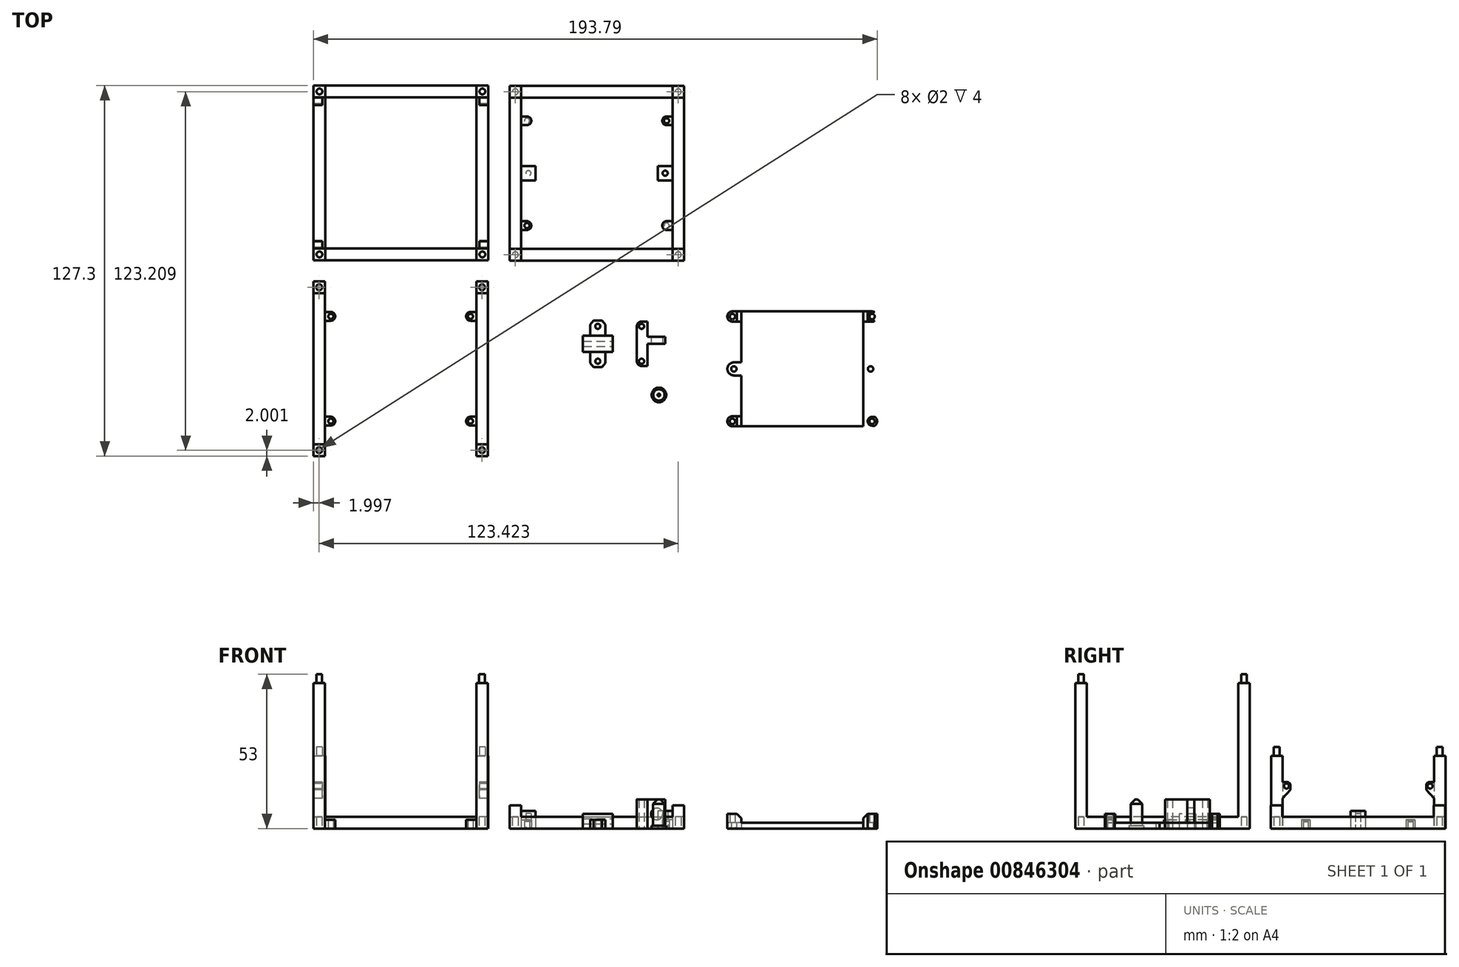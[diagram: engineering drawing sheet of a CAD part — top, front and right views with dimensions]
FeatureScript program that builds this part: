
annotation { "Feature Type Name" : "Feature", "Feature Type Description" : "" }
export const myFeature = defineFeature(function(context is Context, id is Id, definition is map)
    precondition{}
    {
        {
            var Q0;
            Q0=qCreatedBy(makeId("Top.planeOp"),FACE);
            var sketch = newSketch(context, id + "F0", { "sketchPlane" : qUnion([Q0])});
            skLineSegment(sketch, "E0.bottom", {"start": v(0, 60) * mm, "end": v(60, 60) * mm});
            skLineSegment(sketch, "E0.top", {"start": v(0, 0) * mm, "end": v(60, 0) * mm});
            skLineSegment(sketch, "E0.left", {"start": v(0, 60) * mm, "end": v(0, 0) * mm});
            skLineSegment(sketch, "E0.right", {"start": v(60, 60) * mm, "end": v(60, 0) * mm});
            skLineSegment(sketch, "E1.bottom", {"start": v(4, 56) * mm, "end": v(56, 56) * mm});
            skLineSegment(sketch, "E1.top", {"start": v(4, 4) * mm, "end": v(56, 4) * mm});
            skLineSegment(sketch, "E1.left", {"start": v(4, 56) * mm, "end": v(4, 4) * mm});
            skLineSegment(sketch, "E1.right", {"start": v(56, 56) * mm, "end": v(56, 4) * mm});
            skLineSegment(sketch, "E2", {"start": v(4, 56) * mm, "end": v(4, 60) * mm});
            skLineSegment(sketch, "E3", {"start": v(4, 56) * mm, "end": v(0, 56) * mm});
            skLineSegment(sketch, "E4", {"start": v(56, 56) * mm, "end": v(60, 56) * mm});
            skLineSegment(sketch, "E5", {"start": v(56, 56) * mm, "end": v(56, 60) * mm});
            skLineSegment(sketch, "E6", {"start": v(56, 4) * mm, "end": v(60, 4) * mm});
            skLineSegment(sketch, "E7", {"start": v(56, 4) * mm, "end": v(56, 0) * mm});
            skLineSegment(sketch, "E8", {"start": v(4, 4) * mm, "end": v(4, 0) * mm});
            skLineSegment(sketch, "E9", {"start": v(4, 4) * mm, "end": v(0, 4) * mm});
            skCircle(sketch, "E10", {"center": v(2, 58) * mm, "radius": 1 * mm});
            skPoint(sketch, "E10.centerSnap0", {"position": v(4, 58) * mm});
            skPoint(sketch, "E10.centerSnap1", {"position": v(2, 56) * mm});
            skCircle(sketch, "E11", {"center": v(58, 58) * mm, "radius": 1 * mm});
            skPoint(sketch, "E11.centerSnap0", {"position": v(56, 58) * mm});
            skPoint(sketch, "E11.centerSnap1", {"position": v(58, 56) * mm});
            skCircle(sketch, "E12", {"center": v(58, 2) * mm, "radius": 1 * mm});
            skPoint(sketch, "E12.centerSnap0", {"position": v(58, 4) * mm});
            skPoint(sketch, "E12.centerSnap1", {"position": v(56, 2) * mm});
            skCircle(sketch, "E13", {"center": v(2, 2) * mm, "radius": 1 * mm});
            skPoint(sketch, "E13.centerSnap0", {"position": v(2, 4) * mm});
            skPoint(sketch, "E13.centerSnap1", {"position": v(4, 2) * mm});
            skLineSegment(sketch, "E14", {"start": v(4, 49.5) * mm, "end": v(6, 49.5) * mm});
            skLineSegment(sketch, "E15", {"start": v(4, 46.5) * mm, "end": v(6, 46.5) * mm});
            skArc(sketch, "E16", {"start": v(6, 49.5) * mm, "mid": v(7.5, 48) * mm, "end": v(6, 46.5) * mm});
            skCircle(sketch, "E17", {"center": v(6, 48) * mm, "radius": 0.88 * mm});
            skPoint(sketch, "E18", {"position": v(4, 30) * mm});
            skLineSegment(sketch, "E19", {"start": v(-2.87, 30) * mm, "end": v(61.33, 30) * mm, "construction": true});
            skPoint(sketch, "E20", {"position": v(30, 56) * mm});
            skLineSegment(sketch, "E21", {"start": v(30, 61.27) * mm, "end": v(30, -1.45) * mm, "construction": true});
            skPoint(sketch, "E21.endSnap0", {"position": v(30, 0) * mm});
            skArc(sketch, "E22.MirrorCS", {"start": v(54, 49.5) * mm, "mid": v(52.5, 48) * mm, "end": v(54, 46.5) * mm});
            skLineSegment(sketch, "E23.MirrorCS", {"start": v(56, 46.5) * mm, "end": v(54, 46.5) * mm});
            skLineSegment(sketch, "E24.MirrorCS", {"start": v(56, 49.5) * mm, "end": v(54, 49.5) * mm});
            skCircle(sketch, "E25.MirrorC", {"center": v(54, 48) * mm, "radius": 0.88 * mm});
            skLineSegment(sketch, "E26.MirrorCS", {"start": v(56, 10.5) * mm, "end": v(54, 10.5) * mm});
            skLineSegment(sketch, "E27.MirrorCS", {"start": v(56, 13.5) * mm, "end": v(54, 13.5) * mm});
            skCircle(sketch, "E28.MirrorC", {"center": v(54, 12) * mm, "radius": 0.88 * mm});
            skArc(sketch, "E29.MirrorCS", {"start": v(54, 10.5) * mm, "mid": v(52.5, 12) * mm, "end": v(54, 13.5) * mm});
            skArc(sketch, "E30.MirrorCS", {"start": v(6, 10.5) * mm, "mid": v(7.5, 12) * mm, "end": v(6, 13.5) * mm});
            skLineSegment(sketch, "E31.MirrorCS", {"start": v(4, 13.5) * mm, "end": v(6, 13.5) * mm});
            skLineSegment(sketch, "E32.MirrorCS", {"start": v(4, 10.5) * mm, "end": v(6, 10.5) * mm});
            skCircle(sketch, "E33.MirrorC", {"center": v(6, 12) * mm, "radius": 0.88 * mm});
            skLineSegment(sketch, "E34", {"start": v(4, 32.5) * mm, "end": v(9, 32.5) * mm});
            skLineSegment(sketch, "E35", {"start": v(9, 32.5) * mm, "end": v(9, 30) * mm});
            skPoint(sketch, "E36", {"position": v(6.5, 32.5) * mm});
            skLineSegment(sketch, "E37.MirrorCS", {"start": v(9, 27.5) * mm, "end": v(9, 30) * mm});
            skLineSegment(sketch, "E38.MirrorCS", {"start": v(4, 27.5) * mm, "end": v(9, 27.5) * mm});
            skLineSegment(sketch, "E39.MirrorCS", {"start": v(56, 27.5) * mm, "end": v(51, 27.5) * mm});
            skLineSegment(sketch, "E40.MirrorCS", {"start": v(51, 27.5) * mm, "end": v(51, 30) * mm});
            skLineSegment(sketch, "E41.MirrorCS", {"start": v(56, 32.5) * mm, "end": v(51, 32.5) * mm});
            skLineSegment(sketch, "E42.MirrorCS", {"start": v(51, 32.5) * mm, "end": v(51, 30) * mm});
            skCircle(sketch, "E43", {"center": v(6.5, 30) * mm, "radius": 0.88 * mm});
            skCircle(sketch, "E44.MirrorC", {"center": v(53.5, 30) * mm, "radius": 0.88 * mm});
            skSolve(sketch);
        }
        {
            var Q0;
            Q0=makeQuery(id+"F0.imprint","IMPRINT",FACE,{"disambiguationData":[TD([[makeQuery(id+"F0.imprint","IMPRINT",EDGE,{"derivedFrom":sQuery(id+"F0.wireOp",EDGE,"E1.bottom")}),1.0]])]});
            var Q1;
            Q1=makeQuery(id+"F0.imprint","IMPRINT",FACE,{"disambiguationData":[TD([[makeQuery(id+"F0.imprint","IMPRINT",EDGE,{"derivedFrom":sQuery(id+"F0.wireOp",EDGE,"E1.right")}),1.0]])]});
            var Q2;
            {var subQ4=sQuery(id+"F0.wireOp",EDGE,"E6");Q2=makeQuery(id+"F0.imprint","IMPRINT",FACE,{"disambiguationData":[TD([[makeQuery(id+"F0.imprint","IMPRINT",EDGE,{"derivedFrom":subQ4}),-1.0]])]});}
            var Q3;
            {var subQ0=sQuery(id+"F0.wireOp",EDGE,"E8");Q3=makeQuery(id+"F0.imprint","IMPRINT",FACE,{"disambiguationData":[TD([[makeQuery(id+"F0.imprint","IMPRINT",EDGE,{"derivedFrom":subQ0}),-1.0]])]});}
            var Q4;
            Q4=makeQuery(id+"F0.imprint","IMPRINT",FACE,{"disambiguationData":[TD([[makeQuery(id+"F0.imprint","IMPRINT",EDGE,{"derivedFrom":sQuery(id+"F0.wireOp",EDGE,"E1.left")}),-1.0]])]});
            var Q5;
            Q5=makeQuery(id+"F0.imprint","IMPRINT",FACE,{"disambiguationData":[TD([[makeQuery(id+"F0.imprint","IMPRINT",EDGE,{"derivedFrom":sQuery(id+"F0.wireOp",EDGE,"E1.top")}),-1.0]])]});
            var Q6;
            {var subQ4=sQuery(id+"F0.wireOp",EDGE,"E2");Q6=makeQuery(id+"F0.imprint","IMPRINT",FACE,{"disambiguationData":[TD([[makeQuery(id+"F0.imprint","IMPRINT",EDGE,{"derivedFrom":subQ4}),1.0]])]});}
            var Q7;
            {var subQ0=sQuery(id+"F0.wireOp",EDGE,"E4");Q7=makeQuery(id+"F0.imprint","IMPRINT",FACE,{"disambiguationData":[TD([[makeQuery(id+"F0.imprint","IMPRINT",EDGE,{"derivedFrom":subQ0}),1.0]])]});}
            extrude(context, id + "F1", {"entities" : qUnion([Q0, Q1, Q2, Q3, Q4, Q5, Q6, Q7]), "depth" : 4 * mm, "offsetDistance" : 25 * mm});
        }
        {
            var Q0;
            {var subQ4=sQuery(id+"F0.wireOp",EDGE,"E6");Q0=makeQuery(id+"F0.imprint","IMPRINT",FACE,{"disambiguationData":[TD([[makeQuery(id+"F0.imprint","IMPRINT",EDGE,{"derivedFrom":subQ4}),-1.0]])]});}
            var Q1;
            Q1=makeQuery(id+"F0.imprint","IMPRINT",FACE,{"disambiguationData":[TD([[makeQuery(id+"F0.imprint","IMPRINT",EDGE,{"derivedFrom":sQuery(id+"F0.wireOp",EDGE,"E12")}),1.0]])]});
            var Q2;
            Q2=makeQuery(id+"F0.imprint","IMPRINT",FACE,{"disambiguationData":[TD([[makeQuery(id+"F0.imprint","IMPRINT",EDGE,{"derivedFrom":sQuery(id+"F0.wireOp",EDGE,"E13")}),1.0]])]});
            var Q3;
            {var subQ0=sQuery(id+"F0.wireOp",EDGE,"E8");Q3=makeQuery(id+"F0.imprint","IMPRINT",FACE,{"disambiguationData":[TD([[makeQuery(id+"F0.imprint","IMPRINT",EDGE,{"derivedFrom":subQ0}),-1.0]])]});}
            var Q4;
            Q4=makeQuery(id+"F0.imprint","IMPRINT",FACE,{"disambiguationData":[TD([[makeQuery(id+"F0.imprint","IMPRINT",EDGE,{"derivedFrom":sQuery(id+"F0.wireOp",EDGE,"E10")}),1.0]])]});
            var Q5;
            {var subQ4=sQuery(id+"F0.wireOp",EDGE,"E2");Q5=makeQuery(id+"F0.imprint","IMPRINT",FACE,{"disambiguationData":[TD([[makeQuery(id+"F0.imprint","IMPRINT",EDGE,{"derivedFrom":subQ4}),1.0]])]});}
            var Q6;
            {var subQ0=sQuery(id+"F0.wireOp",EDGE,"E4");Q6=makeQuery(id+"F0.imprint","IMPRINT",FACE,{"disambiguationData":[TD([[makeQuery(id+"F0.imprint","IMPRINT",EDGE,{"derivedFrom":subQ0}),1.0]])]});}
            var Q7;
            Q7=makeQuery(id+"F0.imprint","IMPRINT",FACE,{"disambiguationData":[TD([[makeQuery(id+"F0.imprint","IMPRINT",EDGE,{"derivedFrom":sQuery(id+"F0.wireOp",EDGE,"E11")}),1.0]])]});
            extrude(context, id + "F2", {"entities" : qUnion([Q0, Q1, Q2, Q3, Q4, Q5, Q6, Q7]), "operationType" : NewBodyOperationType.ADD, "depth" : 8 * mm, "offsetDistance" : 25 * mm});
        }
        {
            var Q0;
            Q0=qCreatedBy(makeId("Top.planeOp"),FACE);
            var sketch = newSketch(context, id + "F3", { "sketchPlane" : qUnion([Q0])});
            skLineSegment(sketch, "E45.bottom", {"start": v(-67.33, 60.09) * mm, "end": v(-7.33, 60.09) * mm});
            skLineSegment(sketch, "E45.top", {"start": v(-67.33, 0.09) * mm, "end": v(-7.33, 0.09) * mm});
            skLineSegment(sketch, "E45.left", {"start": v(-67.33, 60.09) * mm, "end": v(-67.33, 0.09) * mm});
            skLineSegment(sketch, "E45.right", {"start": v(-7.33, 60.09) * mm, "end": v(-7.33, 0.09) * mm});
            skLineSegment(sketch, "E46.bottom", {"start": v(-63.33, 56.09) * mm, "end": v(-11.33, 56.09) * mm});
            skLineSegment(sketch, "E46.top", {"start": v(-63.33, 4.09) * mm, "end": v(-11.33, 4.09) * mm});
            skLineSegment(sketch, "E46.left", {"start": v(-63.33, 56.09) * mm, "end": v(-63.33, 4.09) * mm});
            skLineSegment(sketch, "E46.right", {"start": v(-11.33, 56.09) * mm, "end": v(-11.33, 4.09) * mm});
            skLineSegment(sketch, "E47", {"start": v(-63.33, 56.09) * mm, "end": v(-63.33, 60.09) * mm});
            skLineSegment(sketch, "E48", {"start": v(-63.33, 56.09) * mm, "end": v(-67.33, 56.09) * mm});
            skLineSegment(sketch, "E49", {"start": v(-11.33, 56.09) * mm, "end": v(-7.33, 56.09) * mm});
            skLineSegment(sketch, "E50", {"start": v(-11.33, 56.09) * mm, "end": v(-11.33, 60.09) * mm});
            skLineSegment(sketch, "E51", {"start": v(-11.33, 4.09) * mm, "end": v(-7.33, 4.09) * mm});
            skLineSegment(sketch, "E52", {"start": v(-11.33, 4.09) * mm, "end": v(-11.33, 0.09) * mm});
            skLineSegment(sketch, "E53", {"start": v(-63.33, 4.09) * mm, "end": v(-63.33, 0.09) * mm});
            skLineSegment(sketch, "E54", {"start": v(-63.33, 4.09) * mm, "end": v(-67.33, 4.09) * mm});
            skCircle(sketch, "E55", {"center": v(-65.33, 58.09) * mm, "radius": 1 * mm});
            skPoint(sketch, "E55.centerSnap0", {"position": v(-63.33, 58.09) * mm});
            skPoint(sketch, "E55.centerSnap1", {"position": v(-65.33, 56.09) * mm});
            skCircle(sketch, "E56", {"center": v(-9.33, 58.09) * mm, "radius": 1 * mm});
            skPoint(sketch, "E56.centerSnap0", {"position": v(-11.33, 58.09) * mm});
            skPoint(sketch, "E56.centerSnap1", {"position": v(-9.33, 56.09) * mm});
            skCircle(sketch, "E57", {"center": v(-9.33, 2.09) * mm, "radius": 1 * mm});
            skPoint(sketch, "E57.centerSnap0", {"position": v(-9.33, 4.09) * mm});
            skPoint(sketch, "E57.centerSnap1", {"position": v(-11.33, 2.09) * mm});
            skCircle(sketch, "E58", {"center": v(-65.33, 2.09) * mm, "radius": 1 * mm});
            skPoint(sketch, "E58.centerSnap0", {"position": v(-65.33, 4.09) * mm});
            skPoint(sketch, "E58.centerSnap1", {"position": v(-63.33, 2.09) * mm});
            skSolve(sketch);
        }
        {
            var Q0;
            {var subQ0=sQuery(id+"F3.wireOp",EDGE,"E49");Q0=makeQuery(id+"F3.imprint","IMPRINT",FACE,{"disambiguationData":[TD([[makeQuery(id+"F3.imprint","IMPRINT",EDGE,{"derivedFrom":subQ0}),1.0]])]});}
            var Q1;
            Q1=makeQuery(id+"F3.imprint","IMPRINT",FACE,{"disambiguationData":[TD([[makeQuery(id+"F3.imprint","IMPRINT",EDGE,{"derivedFrom":sQuery(id+"F3.wireOp",EDGE,"E46.right")}),1.0]])]});
            var Q2;
            {var subQ4=sQuery(id+"F3.wireOp",EDGE,"E51");Q2=makeQuery(id+"F3.imprint","IMPRINT",FACE,{"disambiguationData":[TD([[makeQuery(id+"F3.imprint","IMPRINT",EDGE,{"derivedFrom":subQ4}),-1.0]])]});}
            var Q3;
            {var subQ0=sQuery(id+"F3.wireOp",EDGE,"E53");Q3=makeQuery(id+"F3.imprint","IMPRINT",FACE,{"disambiguationData":[TD([[makeQuery(id+"F3.imprint","IMPRINT",EDGE,{"derivedFrom":subQ0}),-1.0]])]});}
            var Q4;
            Q4=makeQuery(id+"F3.imprint","IMPRINT",FACE,{"disambiguationData":[TD([[makeQuery(id+"F3.imprint","IMPRINT",EDGE,{"derivedFrom":sQuery(id+"F3.wireOp",EDGE,"E46.left")}),-1.0]])]});
            var Q5;
            {var subQ4=sQuery(id+"F3.wireOp",EDGE,"E47");Q5=makeQuery(id+"F3.imprint","IMPRINT",FACE,{"disambiguationData":[TD([[makeQuery(id+"F3.imprint","IMPRINT",EDGE,{"derivedFrom":subQ4}),1.0]])]});}
            var Q6;
            Q6=makeQuery(id+"F3.imprint","IMPRINT",FACE,{"disambiguationData":[TD([[makeQuery(id+"F3.imprint","IMPRINT",EDGE,{"derivedFrom":sQuery(id+"F3.wireOp",EDGE,"E46.top")}),-1.0]])]});
            var Q7;
            Q7=makeQuery(id+"F3.imprint","IMPRINT",FACE,{"disambiguationData":[TD([[makeQuery(id+"F3.imprint","IMPRINT",EDGE,{"derivedFrom":sQuery(id+"F3.wireOp",EDGE,"E46.bottom")}),1.0]])]});
            extrude(context, id + "F4", {"entities" : qUnion([Q0, Q1, Q2, Q3, Q4, Q5, Q6, Q7]), "depth" : 4 * mm, "offsetDistance" : 25 * mm});
        }
        {
            var Q0;
            {var subQ0=sQuery(id+"F3.wireOp",EDGE,"E49");Q0=makeQuery(id+"F3.imprint","IMPRINT",FACE,{"disambiguationData":[TD([[makeQuery(id+"F3.imprint","IMPRINT",EDGE,{"derivedFrom":subQ0}),1.0]])]});}
            var Q1;
            {var subQ4=sQuery(id+"F3.wireOp",EDGE,"E47");Q1=makeQuery(id+"F3.imprint","IMPRINT",FACE,{"disambiguationData":[TD([[makeQuery(id+"F3.imprint","IMPRINT",EDGE,{"derivedFrom":subQ4}),1.0]])]});}
            var Q2;
            {var subQ0=sQuery(id+"F3.wireOp",EDGE,"E53");Q2=makeQuery(id+"F3.imprint","IMPRINT",FACE,{"disambiguationData":[TD([[makeQuery(id+"F3.imprint","IMPRINT",EDGE,{"derivedFrom":subQ0}),-1.0]])]});}
            var Q3;
            {var subQ4=sQuery(id+"F3.wireOp",EDGE,"E51");Q3=makeQuery(id+"F3.imprint","IMPRINT",FACE,{"disambiguationData":[TD([[makeQuery(id+"F3.imprint","IMPRINT",EDGE,{"derivedFrom":subQ4}),-1.0]])]});}
            extrude(context, id + "F5", {"entities" : qUnion([Q0, Q1, Q2, Q3]), "operationType" : NewBodyOperationType.ADD, "depth" : 25 * mm, "offsetDistance" : 25 * mm});
        }
        {
            var Q0;
            Q0=makeQuery(id+"F3.imprint","IMPRINT",FACE,{"disambiguationData":[TD([[makeQuery(id+"F3.imprint","IMPRINT",EDGE,{"derivedFrom":sQuery(id+"F3.wireOp",EDGE,"E56")}),1.0]])]});
            var Q1;
            Q1=makeQuery(id+"F3.imprint","IMPRINT",FACE,{"disambiguationData":[TD([[makeQuery(id+"F3.imprint","IMPRINT",EDGE,{"derivedFrom":sQuery(id+"F3.wireOp",EDGE,"E57")}),1.0]])]});
            var Q2;
            Q2=makeQuery(id+"F3.imprint","IMPRINT",FACE,{"disambiguationData":[TD([[makeQuery(id+"F3.imprint","IMPRINT",EDGE,{"derivedFrom":sQuery(id+"F3.wireOp",EDGE,"E58")}),1.0]])]});
            var Q3;
            Q3=makeQuery(id+"F3.imprint","IMPRINT",FACE,{"disambiguationData":[TD([[makeQuery(id+"F3.imprint","IMPRINT",EDGE,{"derivedFrom":sQuery(id+"F3.wireOp",EDGE,"E55")}),1.0]])]});
            extrude(context, id + "F6", {"entities" : qUnion([Q0, Q1, Q2, Q3]), "operationType" : NewBodyOperationType.ADD, "depth" : 28 * mm, "offsetDistance" : 25 * mm});
        }
        {
            var Q0;
            Q0=qCreatedBy(makeId("Top.planeOp"),FACE);
            var sketch = newSketch(context, id + "F7", { "sketchPlane" : qUnion([Q0])});
            skLineSegment(sketch, "E59.bottom", {"start": v(-67.42, -7.2) * mm, "end": v(-7.42, -7.2) * mm});
            skLineSegment(sketch, "E59.top", {"start": v(-67.42, -67.2) * mm, "end": v(-7.42, -67.2) * mm});
            skLineSegment(sketch, "E59.left", {"start": v(-67.42, -7.2) * mm, "end": v(-67.42, -67.2) * mm});
            skLineSegment(sketch, "E59.right", {"start": v(-7.42, -7.2) * mm, "end": v(-7.42, -67.2) * mm});
            skLineSegment(sketch, "E60.bottom", {"start": v(-63.42, -11.2) * mm, "end": v(-11.42, -11.2) * mm});
            skLineSegment(sketch, "E60.top", {"start": v(-63.42, -63.2) * mm, "end": v(-11.42, -63.2) * mm});
            skLineSegment(sketch, "E60.left", {"start": v(-63.42, -11.2) * mm, "end": v(-63.42, -63.2) * mm});
            skLineSegment(sketch, "E60.right", {"start": v(-11.42, -11.2) * mm, "end": v(-11.42, -63.2) * mm});
            skLineSegment(sketch, "E61", {"start": v(-63.42, -11.2) * mm, "end": v(-63.42, -7.2) * mm});
            skLineSegment(sketch, "E62", {"start": v(-63.42, -11.2) * mm, "end": v(-67.42, -11.2) * mm});
            skLineSegment(sketch, "E63", {"start": v(-11.42, -11.2) * mm, "end": v(-7.42, -11.2) * mm});
            skLineSegment(sketch, "E64", {"start": v(-11.42, -11.2) * mm, "end": v(-11.42, -7.2) * mm});
            skLineSegment(sketch, "E65", {"start": v(-11.42, -63.2) * mm, "end": v(-7.42, -63.2) * mm});
            skLineSegment(sketch, "E66", {"start": v(-11.42, -63.2) * mm, "end": v(-11.42, -67.2) * mm});
            skLineSegment(sketch, "E67", {"start": v(-63.42, -63.2) * mm, "end": v(-63.42, -67.2) * mm});
            skLineSegment(sketch, "E68", {"start": v(-63.42, -63.2) * mm, "end": v(-67.42, -63.2) * mm});
            skCircle(sketch, "E69", {"center": v(-65.42, -9.2) * mm, "radius": 1 * mm});
            skPoint(sketch, "E69.centerSnap0", {"position": v(-63.42, -9.2) * mm});
            skPoint(sketch, "E69.centerSnap1", {"position": v(-65.42, -11.2) * mm});
            skCircle(sketch, "E70", {"center": v(-9.42, -9.2) * mm, "radius": 1 * mm});
            skPoint(sketch, "E70.centerSnap0", {"position": v(-11.42, -9.2) * mm});
            skPoint(sketch, "E70.centerSnap1", {"position": v(-9.42, -11.2) * mm});
            skCircle(sketch, "E71", {"center": v(-9.42, -65.2) * mm, "radius": 1 * mm});
            skPoint(sketch, "E71.centerSnap0", {"position": v(-9.42, -63.2) * mm});
            skPoint(sketch, "E71.centerSnap1", {"position": v(-11.42, -65.2) * mm});
            skCircle(sketch, "E72", {"center": v(-65.42, -65.2) * mm, "radius": 1 * mm});
            skPoint(sketch, "E72.centerSnap0", {"position": v(-65.42, -63.2) * mm});
            skPoint(sketch, "E72.centerSnap1", {"position": v(-63.42, -65.2) * mm});
            skLineSegment(sketch, "E73", {"start": v(-63.42, -17.7) * mm, "end": v(-61.42, -17.7) * mm});
            skLineSegment(sketch, "E74", {"start": v(-63.42, -20.7) * mm, "end": v(-61.42, -20.7) * mm});
            skArc(sketch, "E75", {"start": v(-61.42, -17.7) * mm, "mid": v(-59.92, -19.2) * mm, "end": v(-61.42, -20.7) * mm});
            skCircle(sketch, "E76", {"center": v(-61.42, -19.2) * mm, "radius": 0.88 * mm});
            skArc(sketch, "E77.MirrorCS", {"start": v(-13.42, -17.7) * mm, "mid": v(-14.92, -19.2) * mm, "end": v(-13.42, -20.7) * mm});
            skCircle(sketch, "E78.MirrorC", {"center": v(-13.42, -19.2) * mm, "radius": 0.88 * mm});
            skLineSegment(sketch, "E79.MirrorCS", {"start": v(-11.42, -56.7) * mm, "end": v(-13.42, -56.7) * mm});
            skLineSegment(sketch, "E80.MirrorCS", {"start": v(-11.42, -53.7) * mm, "end": v(-13.42, -53.7) * mm});
            skCircle(sketch, "E81.MirrorC", {"center": v(-13.42, -55.2) * mm, "radius": 0.88 * mm});
            skArc(sketch, "E82.MirrorCS", {"start": v(-13.42, -56.7) * mm, "mid": v(-14.92, -55.2) * mm, "end": v(-13.42, -53.7) * mm});
            skArc(sketch, "E83.MirrorCS", {"start": v(-61.42, -56.7) * mm, "mid": v(-59.92, -55.2) * mm, "end": v(-61.42, -53.7) * mm});
            skLineSegment(sketch, "E84.MirrorCS", {"start": v(-63.42, -53.7) * mm, "end": v(-61.42, -53.7) * mm});
            skLineSegment(sketch, "E85.MirrorCS", {"start": v(-63.42, -56.7) * mm, "end": v(-61.42, -56.7) * mm});
            skCircle(sketch, "E86.MirrorC", {"center": v(-61.42, -55.2) * mm, "radius": 0.88 * mm});
            skLineSegment(sketch, "E87.MirrorCS", {"start": v(-11.42, -17.7) * mm, "end": v(-13.42, -17.7) * mm});
            skLineSegment(sketch, "E88.MirrorCS", {"start": v(-11.42, -20.7) * mm, "end": v(-13.42, -20.7) * mm});
            skSolve(sketch);
        }
        {
            var Q0;
            {var subQ4=sQuery(id+"F7.wireOp",EDGE,"E61");Q0=makeQuery(id+"F7.imprint","IMPRINT",FACE,{"disambiguationData":[TD([[makeQuery(id+"F7.imprint","IMPRINT",EDGE,{"derivedFrom":subQ4}),1.0]])]});}
            var Q1;
            Q1=makeQuery(id+"F7.imprint","IMPRINT",FACE,{"disambiguationData":[TD([[makeQuery(id+"F7.imprint","IMPRINT",EDGE,{"derivedFrom":sQuery(id+"F7.wireOp",EDGE,"E60.left")}),-1.0]])]});
            var Q2;
            {var subQ0=sQuery(id+"F7.wireOp",EDGE,"E63");Q2=makeQuery(id+"F7.imprint","IMPRINT",FACE,{"disambiguationData":[TD([[makeQuery(id+"F7.imprint","IMPRINT",EDGE,{"derivedFrom":subQ0}),1.0]])]});}
            var Q3;
            Q3=makeQuery(id+"F7.imprint","IMPRINT",FACE,{"disambiguationData":[TD([[makeQuery(id+"F7.imprint","IMPRINT",EDGE,{"derivedFrom":sQuery(id+"F7.wireOp",EDGE,"E60.right")}),1.0]])]});
            var Q4;
            {var subQ4=sQuery(id+"F7.wireOp",EDGE,"E65");Q4=makeQuery(id+"F7.imprint","IMPRINT",FACE,{"disambiguationData":[TD([[makeQuery(id+"F7.imprint","IMPRINT",EDGE,{"derivedFrom":subQ4}),-1.0]])]});}
            var Q5;
            {var subQ0=sQuery(id+"F7.wireOp",EDGE,"E67");Q5=makeQuery(id+"F7.imprint","IMPRINT",FACE,{"disambiguationData":[TD([[makeQuery(id+"F7.imprint","IMPRINT",EDGE,{"derivedFrom":subQ0}),-1.0]])]});}
            extrude(context, id + "F8", {"entities" : qUnion([Q0, Q1, Q2, Q3, Q4, Q5]), "depth" : 4 * mm, "offsetDistance" : 25 * mm});
        }
        {
            var Q0;
            {var subQ0=sQuery(id+"F7.wireOp",EDGE,"E67");Q0=makeQuery(id+"F7.imprint","IMPRINT",FACE,{"disambiguationData":[TD([[makeQuery(id+"F7.imprint","IMPRINT",EDGE,{"derivedFrom":subQ0}),-1.0]])]});}
            var Q1;
            {var subQ4=sQuery(id+"F7.wireOp",EDGE,"E61");Q1=makeQuery(id+"F7.imprint","IMPRINT",FACE,{"disambiguationData":[TD([[makeQuery(id+"F7.imprint","IMPRINT",EDGE,{"derivedFrom":subQ4}),1.0]])]});}
            var Q2;
            {var subQ0=sQuery(id+"F7.wireOp",EDGE,"E63");Q2=makeQuery(id+"F7.imprint","IMPRINT",FACE,{"disambiguationData":[TD([[makeQuery(id+"F7.imprint","IMPRINT",EDGE,{"derivedFrom":subQ0}),1.0]])]});}
            var Q3;
            {var subQ4=sQuery(id+"F7.wireOp",EDGE,"E65");Q3=makeQuery(id+"F7.imprint","IMPRINT",FACE,{"disambiguationData":[TD([[makeQuery(id+"F7.imprint","IMPRINT",EDGE,{"derivedFrom":subQ4}),-1.0]])]});}
            extrude(context, id + "F9", {"entities" : qUnion([Q0, Q1, Q2, Q3]), "operationType" : NewBodyOperationType.ADD, "depth" : 50 * mm, "offsetDistance" : 25 * mm});
        }
        {
            var Q0;
            Q0=makeQuery(id+"F7.imprint","IMPRINT",FACE,{"disambiguationData":[TD([[makeQuery(id+"F7.imprint","IMPRINT",EDGE,{"derivedFrom":sQuery(id+"F7.wireOp",EDGE,"E69")}),1.0]])]});
            var Q1;
            Q1=makeQuery(id+"F7.imprint","IMPRINT",FACE,{"disambiguationData":[TD([[makeQuery(id+"F7.imprint","IMPRINT",EDGE,{"derivedFrom":sQuery(id+"F7.wireOp",EDGE,"E70")}),1.0]])]});
            var Q2;
            Q2=makeQuery(id+"F7.imprint","IMPRINT",FACE,{"disambiguationData":[TD([[makeQuery(id+"F7.imprint","IMPRINT",EDGE,{"derivedFrom":sQuery(id+"F7.wireOp",EDGE,"E71")}),1.0]])]});
            var Q3;
            Q3=makeQuery(id+"F7.imprint","IMPRINT",FACE,{"disambiguationData":[TD([[makeQuery(id+"F7.imprint","IMPRINT",EDGE,{"derivedFrom":sQuery(id+"F7.wireOp",EDGE,"E72")}),1.0]])]});
            extrude(context, id + "F10", {"entities" : qUnion([Q0, Q1, Q2, Q3]), "operationType" : NewBodyOperationType.ADD, "depth" : 53 * mm, "offsetDistance" : 25 * mm});
        }
        {
            var Q0;
            {var subQ1=sQuery(id+"F0.wireOp",EDGE,"E14");Q0=makeQuery(id+"F0.imprint","IMPRINT",FACE,{"disambiguationData":[TD([[makeQuery(id+"F0.imprint","IMPRINT",EDGE,{"derivedFrom":subQ1}),-1.0]])]});}
            var Q1;
            Q1=makeQuery(id+"F0.imprint","IMPRINT",FACE,{"disambiguationData":[TD([[makeQuery(id+"F0.imprint","IMPRINT",EDGE,{"derivedFrom":sQuery(id+"F0.wireOp",EDGE,"E30.MirrorCS")}),1.0]])]});
            var Q2;
            {var subQ1=sQuery(id+"F0.wireOp",EDGE,"E26.MirrorCS");Q2=makeQuery(id+"F0.imprint","IMPRINT",FACE,{"disambiguationData":[TD([[makeQuery(id+"F0.imprint","IMPRINT",EDGE,{"derivedFrom":subQ1}),-1.0]])]});}
            var Q3;
            {var subQ0=sQuery(id+"F0.wireOp",EDGE,"E23.MirrorCS");Q3=makeQuery(id+"F0.imprint","IMPRINT",FACE,{"disambiguationData":[TD([[makeQuery(id+"F0.imprint","IMPRINT",EDGE,{"derivedFrom":subQ0}),-1.0]])]});}
            extrude(context, id + "F11", {"entities" : qUnion([Q0, Q1, Q2, Q3]), "operationType" : NewBodyOperationType.ADD, "depth" : 3 * mm, "offsetDistance" : 25 * mm});
        }
        {
            var Q0;
            {var subQ0=sQuery(id+"F0.wireOp",EDGE,"E34");Q0=makeQuery(id+"F0.imprint","IMPRINT",FACE,{"disambiguationData":[TD([[makeQuery(id+"F0.imprint","IMPRINT",EDGE,{"derivedFrom":subQ0}),-1.0]])]});}
            var Q1;
            {var subQ1=sQuery(id+"F0.wireOp",EDGE,"E39.MirrorCS");Q1=makeQuery(id+"F0.imprint","IMPRINT",FACE,{"disambiguationData":[TD([[makeQuery(id+"F0.imprint","IMPRINT",EDGE,{"derivedFrom":subQ1}),-1.0]])]});}
            extrude(context, id + "F12", {"entities" : qUnion([Q0, Q1]), "operationType" : NewBodyOperationType.ADD, "depth" : 6 * mm, "offsetDistance" : 25 * mm});
        }
        {
            var Q0;
            Q0=makeQuery(id+"F0.imprint","IMPRINT",FACE,{"disambiguationData":[TD([[makeQuery(id+"F0.imprint","IMPRINT",EDGE,{"derivedFrom":sQuery(id+"F0.wireOp",EDGE,"E25.MirrorC")}),-1.0]])]});
            var Q1;
            Q1=makeQuery(id+"F0.imprint","IMPRINT",FACE,{"disambiguationData":[TD([[makeQuery(id+"F0.imprint","IMPRINT",EDGE,{"derivedFrom":sQuery(id+"F0.wireOp",EDGE,"E28.MirrorC")}),1.0]])]});
            var Q2;
            Q2=makeQuery(id+"F0.imprint","IMPRINT",FACE,{"disambiguationData":[TD([[makeQuery(id+"F0.imprint","IMPRINT",EDGE,{"derivedFrom":sQuery(id+"F0.wireOp",EDGE,"E33.MirrorC")}),-1.0]])]});
            var Q3;
            Q3=makeQuery(id+"F0.imprint","IMPRINT",FACE,{"disambiguationData":[TD([[makeQuery(id+"F0.imprint","IMPRINT",EDGE,{"derivedFrom":sQuery(id+"F0.wireOp",EDGE,"E17")}),1.0]])]});
            extrude(context, id + "F13", {"entities" : qUnion([Q0, Q1, Q2, Q3]), "operationType" : NewBodyOperationType.ADD, "depth" : 3 * mm, "offsetDistance" : 25 * mm, "hasSecondDirection" : true, "secondDirectionOppositeDirection" : false, "secondDirectionDepth" : 2.4 * mm});
        }
        {
            var Q0;
            Q0=makeQuery(id+"F0.imprint","IMPRINT",FACE,{"disambiguationData":[TD([[makeQuery(id+"F0.imprint","IMPRINT",EDGE,{"derivedFrom":sQuery(id+"F0.wireOp",EDGE,"E43")}),1.0]])]});
            var Q1;
            Q1=makeQuery(id+"F0.imprint","IMPRINT",FACE,{"disambiguationData":[TD([[makeQuery(id+"F0.imprint","IMPRINT",EDGE,{"derivedFrom":sQuery(id+"F0.wireOp",EDGE,"E44.MirrorC")}),-1.0]])]});
            extrude(context, id + "F14", {"entities" : qUnion([Q0, Q1]), "operationType" : NewBodyOperationType.ADD, "depth" : 6 * mm, "offsetDistance" : 25 * mm, "hasSecondDirection" : true, "secondDirectionOppositeDirection" : false, "secondDirectionDepth" : 5.2 * mm});
        }
        {
            var Q0;
            Q0=makeQuery(id+"F7.imprint","IMPRINT",FACE,{"disambiguationData":[TD([[makeQuery(id+"F7.imprint","IMPRINT",EDGE,{"derivedFrom":sQuery(id+"F7.wireOp",EDGE,"E77.MirrorCS")}),1.0]])]});
            var Q1;
            {var subQ0=sQuery(id+"F7.wireOp",EDGE,"E79.MirrorCS");Q1=makeQuery(id+"F7.imprint","IMPRINT",FACE,{"disambiguationData":[TD([[makeQuery(id+"F7.imprint","IMPRINT",EDGE,{"derivedFrom":subQ0}),-1.0]])]});}
            var Q2;
            Q2=makeQuery(id+"F7.imprint","IMPRINT",FACE,{"disambiguationData":[TD([[makeQuery(id+"F7.imprint","IMPRINT",EDGE,{"derivedFrom":sQuery(id+"F7.wireOp",EDGE,"E83.MirrorCS")}),1.0]])]});
            var Q3;
            {var subQ1=sQuery(id+"F7.wireOp",EDGE,"E73");Q3=makeQuery(id+"F7.imprint","IMPRINT",FACE,{"disambiguationData":[TD([[makeQuery(id+"F7.imprint","IMPRINT",EDGE,{"derivedFrom":subQ1}),-1.0]])]});}
            extrude(context, id + "F15", {"entities" : qUnion([Q0, Q1, Q2, Q3]), "operationType" : NewBodyOperationType.ADD, "depth" : 3 * mm, "offsetDistance" : 25 * mm});
        }
        {
            var Q0;
            {var subQ0=sQuery(id+"F3.wireOp",EDGE,"E45.left");Q0=makeQuery(id+"F5.boolean.opBoolean","MERGE",FACE,{"derivedFrom":[makeQuery(id+"F4.opExtrude","SWEPT_FACE",FACE,{"disambiguationData":[OSD([subQ0])]}),makeQuery(id+"F5.opExtrude","SWEPT_FACE",FACE,{"disambiguationData":[OSD([subQ0]),TDD([makeQuery(id+"F3.imprint","IMPRINT",EDGE,{"disambiguationData":[TD([[makeQuery(id+"F3.imprint","INTERSECT",VERTEX,{"derivedFrom":[sQuery(id+"F3.wireOp",EDGE,"E45.bottom"),subQ0]}),-1.0]])],"derivedFrom":subQ0})])]}),makeQuery(id+"F5.opExtrude","SWEPT_FACE",FACE,{"disambiguationData":[OSD([subQ0]),TDD([makeQuery(id+"F3.imprint","IMPRINT",EDGE,{"disambiguationData":[TD([[makeQuery(id+"F3.imprint","INTERSECT",VERTEX,{"derivedFrom":[sQuery(id+"F3.wireOp",EDGE,"E45.top"),subQ0]}),1.0]])],"derivedFrom":subQ0})])]})]});}
            var sketch = newSketch(context, id + "F16", { "sketchPlane" : qUnion([Q0])});
            skLineSegment(sketch, "E89", {"start": v(-4.09, 10.31) * mm, "end": v(-6.73, 13.26) * mm});
            skLineSegment(sketch, "E90", {"start": v(-6.73, 13.26) * mm, "end": v(-6.73, 14.92) * mm});
            skLineSegment(sketch, "E91", {"start": v(-5.73, 15.92) * mm, "end": v(-4.09, 15.92) * mm});
            skCircle(sketch, "E92", {"center": v(-5.4, 14.6) * mm, "radius": 0.88 * mm});
            skPoint(sketch, "E92.centerSnap0", {"position": v(-5.4, 15.92) * mm});
            skPoint(sketch, "E92.centerSnap1", {"position": v(-6.73, 14.6) * mm});
            skLineSegment(sketch, "E93", {"start": v(-30.09, -2.13) * mm, "end": v(-30.09, 32.03) * mm, "construction": true});
            skPoint(sketch, "E93.startSnap0", {"position": v(-30.09, 0) * mm});
            skPoint(sketch, "E93.endSnap0", {"position": v(-30.09, 4) * mm});
            skLineSegment(sketch, "E94.MirrorCS", {"start": v(-54.45, 15.92) * mm, "end": v(-56.09, 15.92) * mm});
            skCircle(sketch, "E95.MirrorC", {"center": v(-54.77, 14.6) * mm, "radius": 0.88 * mm});
            skLineSegment(sketch, "E96.MirrorCS", {"start": v(-56.09, 10.31) * mm, "end": v(-53.45, 13.26) * mm});
            skLineSegment(sketch, "E97.MirrorCS", {"start": v(-53.45, 13.26) * mm, "end": v(-53.45, 14.92) * mm});
            skPoint(sketch, "E98.MirrorP", {"position": v(-53.45, 14.6) * mm});
            skPoint(sketch, "E99.MirrorP", {"position": v(-54.77, 15.92) * mm});
            skPoint(sketch, "E100.visualSharp", {"position": v(-53.45, 15.92) * mm});
            skArc(sketch, "E100.filletArc", {"start": v(-53.45, 14.92) * mm, "mid": v(-53.74, 15.62) * mm, "end": v(-54.45, 15.92) * mm});
            skPoint(sketch, "E101.visualSharp", {"position": v(-6.73, 15.92) * mm});
            skArc(sketch, "E101.filletArc", {"start": v(-5.73, 15.92) * mm, "mid": v(-6.44, 15.62) * mm, "end": v(-6.73, 14.92) * mm});
            skSolve(sketch);
        }
        {
            var Q0;
            {var subQ0=sQuery(id+"F16.wireOp",EDGE,"E94.MirrorCS");Q0=makeQuery(id+"F16.imprint","IMPRINT",FACE,{"disambiguationData":[TD([[makeQuery(id+"F16.imprint","IMPRINT",EDGE,{"derivedFrom":subQ0}),1.0]])]});}
            var Q1;
            {var subQ1=sQuery(id+"F16.wireOp",EDGE,"d672ee34-3f00-4551-98e5-afc0bb2b90d5.MirrorCS");Q1=makeQuery(id+"F16.imprint","IMPRINT",FACE,{"disambiguationData":[TD([[makeQuery(id+"F16.imprint","IMPRINT",EDGE,{"derivedFrom":subQ1}),1.0]])]});}
            var Q2;
            {var subQ0=sQuery(id+"F16.wireOp",EDGE,"a031e210-9444-4c61-8e33-6fc4722089cd");Q2=makeQuery(id+"F16.imprint","IMPRINT",FACE,{"disambiguationData":[TD([[makeQuery(id+"F16.imprint","IMPRINT",EDGE,{"derivedFrom":subQ0}),-1.0]])]});}
            var Q3;
            {var subQ1=sQuery(id+"F16.wireOp",EDGE,"E89");Q3=makeQuery(id+"F16.imprint","IMPRINT",FACE,{"disambiguationData":[TD([[makeQuery(id+"F16.imprint","IMPRINT",EDGE,{"derivedFrom":subQ1}),-1.0]])]});}
            extrude(context, id + "F17", {"entities" : qUnion([Q0, Q1, Q2, Q3]), "operationType" : NewBodyOperationType.ADD, "oppositeDirection" : true, "depth" : 3 * mm, "offsetDistance" : 25 * mm});
        }
        {
            var Q0;
            {var subQ1=sQuery(id+"F16.wireOp",EDGE,"d672ee34-3f00-4551-98e5-afc0bb2b90d5.MirrorCS");Q0=makeQuery(id+"F16.imprint","IMPRINT",FACE,{"disambiguationData":[TD([[makeQuery(id+"F16.imprint","IMPRINT",EDGE,{"derivedFrom":subQ1}),1.0]])]});}
            var Q1;
            {var subQ0=sQuery(id+"F16.wireOp",EDGE,"E94.MirrorCS");Q1=makeQuery(id+"F16.imprint","IMPRINT",FACE,{"disambiguationData":[TD([[makeQuery(id+"F16.imprint","IMPRINT",EDGE,{"derivedFrom":subQ0}),1.0]])]});}
            var Q2;
            {var subQ1=sQuery(id+"F16.wireOp",EDGE,"E89");Q2=makeQuery(id+"F16.imprint","IMPRINT",FACE,{"disambiguationData":[TD([[makeQuery(id+"F16.imprint","IMPRINT",EDGE,{"derivedFrom":subQ1}),-1.0]])]});}
            var Q3;
            {var subQ0=sQuery(id+"F16.wireOp",EDGE,"a031e210-9444-4c61-8e33-6fc4722089cd");Q3=makeQuery(id+"F16.imprint","IMPRINT",FACE,{"disambiguationData":[TD([[makeQuery(id+"F16.imprint","IMPRINT",EDGE,{"derivedFrom":subQ0}),-1.0]])]});}
            extrude(context, id + "F18", {"entities" : qUnion([Q0, Q1, Q2, Q3]), "operationType" : NewBodyOperationType.ADD, "oppositeDirection" : true, "depth" : 60 * mm, "offsetDistance" : 25 * mm, "hasSecondDirection" : true, "secondDirectionOppositeDirection" : true, "secondDirectionDepth" : 57 * mm});
        }
        {
            var Q0;
            Q0=qCreatedBy(makeId("Top.planeOp"),FACE);
            var sketch = newSketch(context, id + "F19", { "sketchPlane" : qUnion([Q0])});
            skLineSegment(sketch, "E102", {"start": v(30.36, -15.84) * mm, "end": v(30.36, -41.85) * mm, "construction": true});
            skCircle(sketch, "E103", {"center": v(30.36, -22.62) * mm, "radius": 0.88 * mm});
            skCircle(sketch, "E104", {"center": v(30.36, -34.62) * mm, "radius": 0.88 * mm});
            skPoint(sketch, "E105", {"position": v(30.36, -28.62) * mm});
            skLineSegment(sketch, "E106", {"start": v(16.53, -28.62) * mm, "end": v(54, -28.62) * mm, "construction": true});
            skLineSegment(sketch, "E107", {"start": v(30.36, -20.6) * mm, "end": v(28.88, -20.6) * mm});
            skLineSegment(sketch, "E108", {"start": v(28.88, -20.6) * mm, "end": v(27.8, -22.02) * mm});
            skLineSegment(sketch, "E109", {"start": v(27.8, -22.02) * mm, "end": v(27.8, -25.81) * mm});
            skLineSegment(sketch, "E110", {"start": v(27.8, -25.81) * mm, "end": v(25.25, -25.81) * mm});
            skLineSegment(sketch, "E111", {"start": v(25.25, -25.81) * mm, "end": v(25.25, -28.62) * mm});
            skLineSegment(sketch, "E112.MirrorCS", {"start": v(35.47, -25.81) * mm, "end": v(35.47, -28.62) * mm});
            skLineSegment(sketch, "E113.MirrorCS", {"start": v(32.92, -25.81) * mm, "end": v(35.47, -25.81) * mm});
            skLineSegment(sketch, "E114.MirrorCS", {"start": v(32.92, -22.02) * mm, "end": v(32.92, -25.81) * mm});
            skLineSegment(sketch, "E115.MirrorCS", {"start": v(30.36, -20.6) * mm, "end": v(31.84, -20.6) * mm});
            skLineSegment(sketch, "E116.MirrorCS", {"start": v(31.84, -20.6) * mm, "end": v(32.92, -22.02) * mm});
            skLineSegment(sketch, "E117.MirrorCS", {"start": v(44.19, -28.62) * mm, "end": v(6.72, -28.62) * mm, "construction": true});
            skLineSegment(sketch, "E118.MirrorCS", {"start": v(25.25, -31.43) * mm, "end": v(25.25, -28.62) * mm});
            skLineSegment(sketch, "E119.MirrorCS", {"start": v(27.8, -31.43) * mm, "end": v(25.25, -31.43) * mm});
            skLineSegment(sketch, "E120.MirrorCS", {"start": v(27.8, -35.23) * mm, "end": v(27.8, -31.43) * mm});
            skLineSegment(sketch, "E121.MirrorCS", {"start": v(28.88, -36.65) * mm, "end": v(27.8, -35.23) * mm});
            skLineSegment(sketch, "E122.MirrorCS", {"start": v(30.36, -36.65) * mm, "end": v(28.88, -36.65) * mm});
            skLineSegment(sketch, "E123.MirrorCS", {"start": v(30.36, -36.65) * mm, "end": v(31.84, -36.65) * mm});
            skLineSegment(sketch, "E124.MirrorCS", {"start": v(31.84, -36.65) * mm, "end": v(32.92, -35.23) * mm});
            skLineSegment(sketch, "E125.MirrorCS", {"start": v(32.92, -35.23) * mm, "end": v(32.92, -31.43) * mm});
            skLineSegment(sketch, "E126.MirrorCS", {"start": v(35.47, -31.43) * mm, "end": v(35.47, -28.62) * mm});
            skLineSegment(sketch, "E127.MirrorCS", {"start": v(32.92, -31.43) * mm, "end": v(35.47, -31.43) * mm});
            skLineSegment(sketch, "E128", {"start": v(27.8, -25.81) * mm, "end": v(32.92, -25.81) * mm});
            skLineSegment(sketch, "E129", {"start": v(32.92, -31.43) * mm, "end": v(27.8, -31.43) * mm});
            skCircle(sketch, "E130", {"center": v(45.4, -22.62) * mm, "radius": 0.88 * mm});
            skCircle(sketch, "E131", {"center": v(45.4, -34.62) * mm, "radius": 0.88 * mm});
            skLineSegment(sketch, "E132", {"start": v(45.4, -15.56) * mm, "end": v(45.4, -41.47) * mm, "construction": true});
            skLineSegment(sketch, "E133", {"start": v(43.76, -22.62) * mm, "end": v(43.76, -34.62) * mm});
            skArc(sketch, "E134", {"start": v(43.76, -22.62) * mm, "mid": v(44.24, -21.47) * mm, "end": v(45.4, -20.99) * mm});
            skArc(sketch, "E135", {"start": v(43.76, -34.62) * mm, "mid": v(44.24, -35.78) * mm, "end": v(45.4, -36.26) * mm});
            skLineSegment(sketch, "E136", {"start": v(45.4, -20.99) * mm, "end": v(47.44, -20.99) * mm});
            skLineSegment(sketch, "E137", {"start": v(47.44, -20.99) * mm, "end": v(47.44, -36.26) * mm});
            skLineSegment(sketch, "E138", {"start": v(47.44, -36.26) * mm, "end": v(45.4, -36.26) * mm});
            skLineSegment(sketch, "E139", {"start": v(47.44, -26.23) * mm, "end": v(53.5, -26.23) * mm});
            skLineSegment(sketch, "E140", {"start": v(53.5, -26.23) * mm, "end": v(53.5, -28.62) * mm});
            skLineSegment(sketch, "E141", {"start": v(53.5, -28.62) * mm, "end": v(47.44, -28.62) * mm});
            skSolve(sketch);
        }
        {
            var Q0;
            Q0=makeQuery(id+"F19.imprint","IMPRINT",FACE,{"disambiguationData":[TD([[makeQuery(id+"F19.imprint","IMPRINT",EDGE,{"derivedFrom":sQuery(id+"F19.wireOp",EDGE,"E103")}),-1.0]])]});
            var Q1;
            Q1=makeQuery(id+"F19.imprint","IMPRINT",FACE,{"disambiguationData":[TD([[makeQuery(id+"F19.imprint","IMPRINT",EDGE,{"derivedFrom":sQuery(id+"F19.wireOp",EDGE,"E104")}),-1.0]])]});
            var Q2;
            Q2=makeQuery(id+"F19.imprint","IMPRINT",FACE,{"disambiguationData":[TD([[makeQuery(id+"F19.imprint","IMPRINT",EDGE,{"derivedFrom":sQuery(id+"F19.wireOp",EDGE,"E110")}),1.0]])]});
            extrude(context, id + "F20", {"entities" : qUnion([Q0, Q1, Q2]), "depth" : 3 * mm, "offsetDistance" : 25 * mm});
        }
        {
            var Q0;
            Q0=makeQuery(id+"F19.imprint","IMPRINT",FACE,{"disambiguationData":[TD([[makeQuery(id+"F19.imprint","IMPRINT",EDGE,{"derivedFrom":sQuery(id+"F19.wireOp",EDGE,"E110")}),1.0]])]});
            extrude(context, id + "F21", {"entities" : qUnion([Q0]), "operationType" : NewBodyOperationType.ADD, "depth" : 5 * mm, "offsetDistance" : 25 * mm});
        }
        {
            var Q0;
            {var subQ0=sQuery(id+"F19.wireOp",EDGE,"E126.MirrorCS");var subQ1=sQuery(id+"F19.wireOp",EDGE,"E112.MirrorCS");Q0=makeQuery(id+"F21.boolean.opBoolean","MERGE",FACE,{"derivedFrom":[makeQuery(id+"F20.opExtrude","SWEPT_FACE",FACE,{"disambiguationData":[OSD([subQ1,subQ0])]}),makeQuery(id+"F21.opExtrude","SWEPT_FACE",FACE,{"disambiguationData":[OSD([subQ1,subQ0])]})]});}
            var sketch = newSketch(context, id + "F22", { "sketchPlane" : qUnion([Q0])});
            skCircle(sketch, "E142", {"center": v(-28.62, 2.45) * mm, "radius": 0.88 * mm});
            skPoint(sketch, "E142.centerSnap0", {"position": v(-28.62, 0) * mm});
            skSolve(sketch);
        }
        {
            var Q0;
            Q0=makeQuery(id+"F22.imprint","IMPRINT",FACE,{"disambiguationData":[TD([[makeQuery(id+"F22.imprint","IMPRINT",EDGE,{"derivedFrom":sQuery(id+"F22.wireOp",EDGE,"E142")}),1.0]])]});
            extrude(context, id + "F23", {"entities" : qUnion([Q0]), "operationType" : NewBodyOperationType.REMOVE, "oppositeDirection" : true, "depth" : 11 * mm, "offsetDistance" : 25 * mm});
        }
        {
            var Q0;
            Q0=makeQuery(id+"F19.imprint","IMPRINT",FACE,{"disambiguationData":[TD([[makeQuery(id+"F19.imprint","IMPRINT",EDGE,{"derivedFrom":sQuery(id+"F19.wireOp",EDGE,"E130")}),-1.0]])]});
            var Q1;
            {var subQ0=sQuery(id+"F19.wireOp",EDGE,"E139");Q1=makeQuery(id+"F19.imprint","IMPRINT",FACE,{"disambiguationData":[TD([[makeQuery(id+"F19.imprint","IMPRINT",EDGE,{"derivedFrom":subQ0}),-1.0]])]});}
            extrude(context, id + "F24", {"entities" : qUnion([Q0, Q1]), "depth" : 10 * mm, "offsetDistance" : 25 * mm});
        }
        {
            var Q0;
            Q0=makeQuery(id+"F24.opExtrude","SWEPT_FACE",FACE,{"disambiguationData":[OSD([sQuery(id+"F19.wireOp",EDGE,"E141")])]});
            var sketch = newSketch(context, id + "F25", { "sketchPlane" : qUnion([Q0])});
            skCircle(sketch, "E143", {"center": v(50.65, 5) * mm, "radius": 2 * mm});
            skPoint(sketch, "E143.centerSnap0", {"position": v(53.5, 5) * mm});
            skSolve(sketch);
        }
        {
            var Q0;
            Q0=makeQuery(id+"F25.imprint","IMPRINT",FACE,{"disambiguationData":[TD([[makeQuery(id+"F25.imprint","IMPRINT",EDGE,{"derivedFrom":sQuery(id+"F25.wireOp",EDGE,"E143")}),1.0]])]});
            extrude(context, id + "F26", {"entities" : qUnion([Q0]), "operationType" : NewBodyOperationType.REMOVE, "oppositeDirection" : true, "depth" : 10 * mm, "offsetDistance" : 25 * mm});
        }
        {
            var Q0;
            Q0=makeQuery(id+"F0.imprint","IMPRINT",FACE,{"disambiguationData":[TD([[makeQuery(id+"F0.imprint","IMPRINT",EDGE,{"derivedFrom":sQuery(id+"F0.wireOp",EDGE,"E13")}),1.0]])]});
            var Q1;
            Q1=makeQuery(id+"F0.imprint","IMPRINT",FACE,{"disambiguationData":[TD([[makeQuery(id+"F0.imprint","IMPRINT",EDGE,{"derivedFrom":sQuery(id+"F0.wireOp",EDGE,"E12")}),1.0]])]});
            var Q2;
            Q2=makeQuery(id+"F0.imprint","IMPRINT",FACE,{"disambiguationData":[TD([[makeQuery(id+"F0.imprint","IMPRINT",EDGE,{"derivedFrom":sQuery(id+"F0.wireOp",EDGE,"E10")}),1.0]])]});
            var Q3;
            Q3=makeQuery(id+"F0.imprint","IMPRINT",FACE,{"disambiguationData":[TD([[makeQuery(id+"F0.imprint","IMPRINT",EDGE,{"derivedFrom":sQuery(id+"F0.wireOp",EDGE,"E11")}),1.0]])]});
            var Q4;
            Q4=makeQuery(id+"F7.imprint","IMPRINT",FACE,{"disambiguationData":[TD([[makeQuery(id+"F7.imprint","IMPRINT",EDGE,{"derivedFrom":sQuery(id+"F7.wireOp",EDGE,"E70")}),1.0]])]});
            var Q5;
            Q5=makeQuery(id+"F7.imprint","IMPRINT",FACE,{"disambiguationData":[TD([[makeQuery(id+"F7.imprint","IMPRINT",EDGE,{"derivedFrom":sQuery(id+"F7.wireOp",EDGE,"E71")}),1.0]])]});
            var Q6;
            Q6=makeQuery(id+"F7.imprint","IMPRINT",FACE,{"disambiguationData":[TD([[makeQuery(id+"F7.imprint","IMPRINT",EDGE,{"derivedFrom":sQuery(id+"F7.wireOp",EDGE,"E72")}),1.0]])]});
            var Q7;
            Q7=makeQuery(id+"F7.imprint","IMPRINT",FACE,{"disambiguationData":[TD([[makeQuery(id+"F7.imprint","IMPRINT",EDGE,{"derivedFrom":sQuery(id+"F7.wireOp",EDGE,"E69")}),1.0]])]});
            extrude(context, id + "F27", {"entities" : qUnion([Q0, Q1, Q2, Q3, Q4, Q5, Q6, Q7]), "operationType" : NewBodyOperationType.REMOVE, "depth" : 4 * mm, "offsetDistance" : 25 * mm});
        }
        {
            var Q0;
            Q0=qCreatedBy(makeId("Top.planeOp"),FACE);
            var sketch = newSketch(context, id + "F28", { "sketchPlane" : qUnion([Q0])});
            skLineSegment(sketch, "E144.bottom", {"start": v(70.62, -7.27) * mm, "end": v(130.62, -7.27) * mm});
            skLineSegment(sketch, "E144.top", {"start": v(70.62, -67.27) * mm, "end": v(130.62, -67.27) * mm});
            skLineSegment(sketch, "E144.left", {"start": v(70.62, -7.27) * mm, "end": v(70.62, -67.27) * mm});
            skLineSegment(sketch, "E144.right", {"start": v(130.62, -7.27) * mm, "end": v(130.62, -67.27) * mm});
            skLineSegment(sketch, "E145.bottom", {"start": v(74.62, -11.27) * mm, "end": v(126.62, -11.27) * mm});
            skLineSegment(sketch, "E145.top", {"start": v(74.62, -63.27) * mm, "end": v(126.62, -63.27) * mm});
            skLineSegment(sketch, "E145.left", {"start": v(74.62, -11.27) * mm, "end": v(74.62, -63.27) * mm});
            skLineSegment(sketch, "E145.right", {"start": v(126.62, -11.27) * mm, "end": v(126.62, -63.27) * mm});
            skLineSegment(sketch, "E146", {"start": v(74.62, -11.27) * mm, "end": v(74.62, -7.27) * mm});
            skLineSegment(sketch, "E147", {"start": v(74.62, -11.27) * mm, "end": v(70.62, -11.27) * mm});
            skLineSegment(sketch, "E148", {"start": v(126.62, -11.27) * mm, "end": v(130.62, -11.27) * mm});
            skLineSegment(sketch, "E149", {"start": v(126.62, -11.27) * mm, "end": v(126.62, -7.27) * mm});
            skLineSegment(sketch, "E150", {"start": v(126.62, -63.27) * mm, "end": v(130.62, -63.27) * mm});
            skLineSegment(sketch, "E151", {"start": v(126.62, -63.27) * mm, "end": v(126.62, -67.27) * mm});
            skLineSegment(sketch, "E152", {"start": v(74.62, -63.27) * mm, "end": v(74.62, -67.27) * mm});
            skLineSegment(sketch, "E153", {"start": v(74.62, -63.27) * mm, "end": v(70.62, -63.27) * mm});
            skCircle(sketch, "E154", {"center": v(72.62, -9.27) * mm, "radius": 1 * mm});
            skPoint(sketch, "E154.centerSnap0", {"position": v(74.62, -9.27) * mm});
            skPoint(sketch, "E154.centerSnap1", {"position": v(72.62, -11.27) * mm});
            skCircle(sketch, "E155", {"center": v(128.62, -9.27) * mm, "radius": 1 * mm});
            skPoint(sketch, "E155.centerSnap0", {"position": v(126.62, -9.27) * mm});
            skPoint(sketch, "E155.centerSnap1", {"position": v(128.62, -11.27) * mm});
            skCircle(sketch, "E156", {"center": v(128.62, -65.27) * mm, "radius": 1 * mm});
            skPoint(sketch, "E156.centerSnap0", {"position": v(128.62, -63.27) * mm});
            skPoint(sketch, "E156.centerSnap1", {"position": v(126.62, -65.27) * mm});
            skCircle(sketch, "E157", {"center": v(72.62, -65.27) * mm, "radius": 1 * mm});
            skPoint(sketch, "E157.centerSnap0", {"position": v(72.62, -63.27) * mm});
            skPoint(sketch, "E157.centerSnap1", {"position": v(74.62, -65.27) * mm});
            skLineSegment(sketch, "E158", {"start": v(74.62, -17.77) * mm, "end": v(76.62, -17.77) * mm});
            skLineSegment(sketch, "E159", {"start": v(74.62, -20.77) * mm, "end": v(76.62, -20.77) * mm});
            skArc(sketch, "E160", {"start": v(76.62, -17.77) * mm, "mid": v(78.12, -19.27) * mm, "end": v(76.62, -20.77) * mm});
            skCircle(sketch, "E161", {"center": v(76.62, -19.27) * mm, "radius": 0.93 * mm});
            skPoint(sketch, "E162", {"position": v(74.62, -37.27) * mm});
            skLineSegment(sketch, "E163", {"start": v(-33.97, -37.27) * mm, "end": v(30.23, -37.27) * mm, "construction": true});
            skPoint(sketch, "E164", {"position": v(100.62, -11.27) * mm});
            skLineSegment(sketch, "E165", {"start": v(100.62, 29.89) * mm, "end": v(100.62, -32.84) * mm, "construction": true});
            skPoint(sketch, "E165.endSnap0", {"position": v(100.62, -67.27) * mm});
            skArc(sketch, "E166.MirrorCS", {"start": v(124.62, -17.77) * mm, "mid": v(123.12, -19.27) * mm, "end": v(124.62, -20.77) * mm});
            skLineSegment(sketch, "E167.MirrorCS", {"start": v(126.62, -20.77) * mm, "end": v(124.62, -20.77) * mm});
            skLineSegment(sketch, "E168.MirrorCS", {"start": v(126.62, -17.77) * mm, "end": v(124.62, -17.77) * mm});
            skCircle(sketch, "E169.MirrorC", {"center": v(124.62, -19.27) * mm, "radius": 0.93 * mm});
            skLineSegment(sketch, "E170.MirrorCS", {"start": v(126.62, -56.77) * mm, "end": v(124.62, -56.77) * mm});
            skLineSegment(sketch, "E171.MirrorCS", {"start": v(126.62, -53.77) * mm, "end": v(124.62, -53.77) * mm});
            skCircle(sketch, "E172.MirrorC", {"center": v(124.62, -55.27) * mm, "radius": 0.93 * mm});
            skArc(sketch, "E173.MirrorCS", {"start": v(124.62, -56.77) * mm, "mid": v(123.12, -55.27) * mm, "end": v(124.62, -53.77) * mm});
            skArc(sketch, "E174.MirrorCS", {"start": v(76.62, -56.77) * mm, "mid": v(78.12, -55.27) * mm, "end": v(76.62, -53.77) * mm});
            skLineSegment(sketch, "E175.MirrorCS", {"start": v(74.62, -53.77) * mm, "end": v(76.62, -53.77) * mm});
            skLineSegment(sketch, "E176.MirrorCS", {"start": v(74.62, -56.77) * mm, "end": v(76.62, -56.77) * mm});
            skCircle(sketch, "E177.MirrorC", {"center": v(76.62, -55.27) * mm, "radius": 0.93 * mm});
            skLineSegment(sketch, "E178", {"start": v(74.62, -34.77) * mm, "end": v(79.62, -34.77) * mm});
            skLineSegment(sketch, "E179", {"start": v(79.62, -34.77) * mm, "end": v(79.62, -37.27) * mm});
            skPoint(sketch, "E180", {"position": v(77.12, -34.77) * mm});
            skLineSegment(sketch, "E181.MirrorCS", {"start": v(79.62, -39.77) * mm, "end": v(79.62, -37.27) * mm});
            skLineSegment(sketch, "E182.MirrorCS", {"start": v(74.62, -39.77) * mm, "end": v(79.62, -39.77) * mm});
            skLineSegment(sketch, "E183.MirrorCS", {"start": v(126.62, -39.77) * mm, "end": v(121.62, -39.77) * mm});
            skLineSegment(sketch, "E184.MirrorCS", {"start": v(121.62, -39.77) * mm, "end": v(121.62, -37.27) * mm});
            skLineSegment(sketch, "E185.MirrorCS", {"start": v(126.62, -34.77) * mm, "end": v(121.62, -34.77) * mm});
            skLineSegment(sketch, "E186.MirrorCS", {"start": v(121.62, -34.77) * mm, "end": v(121.62, -37.27) * mm});
            skCircle(sketch, "E187", {"center": v(77.12, -37.27) * mm, "radius": 0.93 * mm});
            skCircle(sketch, "E188.MirrorC", {"center": v(124.12, -37.27) * mm, "radius": 0.93 * mm});
            skLineSegment(sketch, "E189.bottom", {"start": v(79.62, -17.52) * mm, "end": v(121.62, -17.52) * mm});
            skLineSegment(sketch, "E189.top", {"start": v(79.62, -57.02) * mm, "end": v(121.62, -57.02) * mm});
            skLineSegment(sketch, "E189.left", {"start": v(79.62, -17.52) * mm, "end": v(79.62, -57.02) * mm});
            skLineSegment(sketch, "E189.right", {"start": v(121.62, -17.52) * mm, "end": v(121.62, -57.02) * mm});
            skLineSegment(sketch, "E190", {"start": v(121.62, -17.52) * mm, "end": v(124.62, -17.52) * mm});
            skLineSegment(sketch, "E191", {"start": v(124.62, -21.02) * mm, "end": v(121.62, -21.02) * mm});
            skArc(sketch, "E192", {"start": v(124.62, -17.52) * mm, "mid": v(126.37, -19.27) * mm, "end": v(124.62, -21.02) * mm});
            skLineSegment(sketch, "E193.MirrorCS", {"start": v(79.62, -17.52) * mm, "end": v(76.62, -17.52) * mm});
            skLineSegment(sketch, "E194.MirrorCS", {"start": v(76.62, -21.02) * mm, "end": v(79.62, -21.02) * mm});
            skArc(sketch, "E195.MirrorCS", {"start": v(76.62, -17.52) * mm, "mid": v(74.86, -19.27) * mm, "end": v(76.62, -21.02) * mm});
            skLineSegment(sketch, "E196.MirrorCS", {"start": v(76.62, -53.52) * mm, "end": v(79.62, -53.52) * mm});
            skArc(sketch, "E197.MirrorCS", {"start": v(76.62, -57.02) * mm, "mid": v(74.86, -55.27) * mm, "end": v(76.62, -53.52) * mm});
            skLineSegment(sketch, "E198.MirrorCS", {"start": v(79.62, -57.02) * mm, "end": v(76.62, -57.02) * mm});
            skLineSegment(sketch, "E199.MirrorCS", {"start": v(124.62, -53.52) * mm, "end": v(121.62, -53.52) * mm});
            skLineSegment(sketch, "E200.MirrorCS", {"start": v(121.62, -57.02) * mm, "end": v(124.62, -57.02) * mm});
            skArc(sketch, "E201.MirrorCS", {"start": v(124.62, -57.02) * mm, "mid": v(126.37, -55.27) * mm, "end": v(124.62, -53.52) * mm});
            skLineSegment(sketch, "E202", {"start": v(121.62, -35.04) * mm, "end": v(124.12, -35.04) * mm});
            skArc(sketch, "E203", {"start": v(124.12, -35.04) * mm, "mid": v(126.34, -37.27) * mm, "end": v(124.12, -39.5) * mm});
            skLineSegment(sketch, "E204", {"start": v(124.12, -39.5) * mm, "end": v(121.62, -39.5) * mm});
            skLineSegment(sketch, "E205.MirrorCS", {"start": v(79.62, -35.04) * mm, "end": v(77.12, -35.04) * mm});
            skLineSegment(sketch, "E206.MirrorCS", {"start": v(77.12, -39.5) * mm, "end": v(79.62, -39.5) * mm});
            skArc(sketch, "E207.MirrorCS", {"start": v(77.12, -35.04) * mm, "mid": v(74.89, -37.27) * mm, "end": v(77.12, -39.5) * mm});
            skCircle(sketch, "E208", {"center": v(51.35, -46.2) * mm, "radius": 2.5 * mm});
            skCircle(sketch, "E209", {"center": v(51.35, -46.2) * mm, "radius": 1.96 * mm});
            skSolve(sketch);
        }
        {
            var Q0;
            {var subQ1=sQuery(id+"F28.wireOp",EDGE,"E189.bottom");Q0=makeQuery(id+"F28.imprint","IMPRINT",FACE,{"disambiguationData":[TD([[makeQuery(id+"F28.imprint","IMPRINT",EDGE,{"derivedFrom":subQ1}),-1.0]])]});}
            var Q1;
            {var subQ3=sQuery(id+"F28.wireOp",EDGE,"E160");Q1=makeQuery(id+"F28.imprint","IMPRINT",FACE,{"disambiguationData":[TD([[makeQuery(id+"F28.imprint","IMPRINT",EDGE,{"derivedFrom":subQ3}),1.0]])]});}
            var Q2;
            {var subQ0=sQuery(id+"F28.wireOp",EDGE,"E160");Q2=makeQuery(id+"F28.imprint","IMPRINT",FACE,{"disambiguationData":[TD([[makeQuery(id+"F28.imprint","IMPRINT",EDGE,{"derivedFrom":subQ0}),-1.0]])]});}
            var Q3;
            Q3=makeQuery(id+"F28.imprint","IMPRINT",FACE,{"disambiguationData":[TD([[makeQuery(id+"F28.imprint","IMPRINT",EDGE,{"derivedFrom":sQuery(id+"F28.wireOp",EDGE,"E187")}),-1.0]])]});
            var Q4;
            {var subQ4=sQuery(id+"F28.wireOp",EDGE,"E174.MirrorCS");Q4=makeQuery(id+"F28.imprint","IMPRINT",FACE,{"disambiguationData":[TD([[makeQuery(id+"F28.imprint","IMPRINT",EDGE,{"derivedFrom":subQ4}),-1.0]])]});}
            var Q5;
            {var subQ1=sQuery(id+"F28.wireOp",EDGE,"E174.MirrorCS");Q5=makeQuery(id+"F28.imprint","IMPRINT",FACE,{"disambiguationData":[TD([[makeQuery(id+"F28.imprint","IMPRINT",EDGE,{"derivedFrom":subQ1}),1.0]])]});}
            var Q6;
            {var subQ3=sQuery(id+"F28.wireOp",EDGE,"E173.MirrorCS");Q6=makeQuery(id+"F28.imprint","IMPRINT",FACE,{"disambiguationData":[TD([[makeQuery(id+"F28.imprint","IMPRINT",EDGE,{"derivedFrom":subQ3}),1.0]])]});}
            var Q7;
            Q7=makeQuery(id+"F28.imprint","IMPRINT",FACE,{"disambiguationData":[TD([[makeQuery(id+"F28.imprint","IMPRINT",EDGE,{"derivedFrom":sQuery(id+"F28.wireOp",EDGE,"E172.MirrorC")}),-1.0]])]});
            var Q8;
            Q8=makeQuery(id+"F28.imprint","IMPRINT",FACE,{"disambiguationData":[TD([[makeQuery(id+"F28.imprint","IMPRINT",EDGE,{"derivedFrom":sQuery(id+"F28.wireOp",EDGE,"E188.MirrorC")}),1.0]])]});
            var Q9;
            Q9=makeQuery(id+"F28.imprint","IMPRINT",FACE,{"disambiguationData":[TD([[makeQuery(id+"F28.imprint","IMPRINT",EDGE,{"derivedFrom":sQuery(id+"F28.wireOp",EDGE,"E169.MirrorC")}),1.0]])]});
            var Q10;
            {var subQ7=sQuery(id+"F28.wireOp",EDGE,"E166.MirrorCS");Q10=makeQuery(id+"F28.imprint","IMPRINT",FACE,{"disambiguationData":[TD([[makeQuery(id+"F28.imprint","IMPRINT",EDGE,{"derivedFrom":subQ7}),-1.0]])]});}
            extrude(context, id + "F29", {"entities" : qUnion([Q0, Q1, Q2, Q3, Q4, Q5, Q6, Q7, Q8, Q9, Q10]), "depth" : 2 * mm, "offsetDistance" : 25 * mm});
        }
        {
            var Q0;
            Q0=makeQuery(id+"F28.imprint","IMPRINT",FACE,{"disambiguationData":[TD([[makeQuery(id+"F28.imprint","IMPRINT",EDGE,{"derivedFrom":sQuery(id+"F28.wireOp",EDGE,"E169.MirrorC")}),1.0]])]});
            var Q1;
            {var subQ7=sQuery(id+"F28.wireOp",EDGE,"E166.MirrorCS");Q1=makeQuery(id+"F28.imprint","IMPRINT",FACE,{"disambiguationData":[TD([[makeQuery(id+"F28.imprint","IMPRINT",EDGE,{"derivedFrom":subQ7}),-1.0]])]});}
            var Q2;
            {var subQ3=sQuery(id+"F28.wireOp",EDGE,"E173.MirrorCS");Q2=makeQuery(id+"F28.imprint","IMPRINT",FACE,{"disambiguationData":[TD([[makeQuery(id+"F28.imprint","IMPRINT",EDGE,{"derivedFrom":subQ3}),1.0]])]});}
            var Q3;
            Q3=makeQuery(id+"F28.imprint","IMPRINT",FACE,{"disambiguationData":[TD([[makeQuery(id+"F28.imprint","IMPRINT",EDGE,{"derivedFrom":sQuery(id+"F28.wireOp",EDGE,"E172.MirrorC")}),-1.0]])]});
            var Q4;
            {var subQ4=sQuery(id+"F28.wireOp",EDGE,"E174.MirrorCS");Q4=makeQuery(id+"F28.imprint","IMPRINT",FACE,{"disambiguationData":[TD([[makeQuery(id+"F28.imprint","IMPRINT",EDGE,{"derivedFrom":subQ4}),-1.0]])]});}
            var Q5;
            {var subQ1=sQuery(id+"F28.wireOp",EDGE,"E174.MirrorCS");Q5=makeQuery(id+"F28.imprint","IMPRINT",FACE,{"disambiguationData":[TD([[makeQuery(id+"F28.imprint","IMPRINT",EDGE,{"derivedFrom":subQ1}),1.0]])]});}
            var Q6;
            {var subQ0=sQuery(id+"F28.wireOp",EDGE,"E160");Q6=makeQuery(id+"F28.imprint","IMPRINT",FACE,{"disambiguationData":[TD([[makeQuery(id+"F28.imprint","IMPRINT",EDGE,{"derivedFrom":subQ0}),-1.0]])]});}
            var Q7;
            {var subQ3=sQuery(id+"F28.wireOp",EDGE,"E160");Q7=makeQuery(id+"F28.imprint","IMPRINT",FACE,{"disambiguationData":[TD([[makeQuery(id+"F28.imprint","IMPRINT",EDGE,{"derivedFrom":subQ3}),1.0]])]});}
            extrude(context, id + "F30", {"entities" : qUnion([Q0, Q1, Q2, Q3, Q4, Q5, Q6, Q7]), "operationType" : NewBodyOperationType.ADD, "depth" : 5 * mm, "offsetDistance" : 25 * mm});
        }
        {
            var Q0;
            {var subQ0=sQuery(id+"F28.wireOp",EDGE,"E189.left");Q0=makeQuery(id+"F30.opExtrude","CAP_EDGE",EDGE,{"disambiguationData":[OSD([subQ0]),TDD([makeQuery(id+"F28.imprint","IMPRINT",EDGE,{"disambiguationData":[TD([[makeQuery(id+"F28.imprint","INTERSECT",VERTEX,{"derivedFrom":[subQ0,sQuery(id+"F28.wireOp",EDGE,"E194.MirrorCS")]}),1.0]])],"derivedFrom":subQ0})])],"isStart":false});}
            var Q1;
            {var subQ0=sQuery(id+"F28.wireOp",EDGE,"E189.right");Q1=makeQuery(id+"F30.opExtrude","CAP_EDGE",EDGE,{"disambiguationData":[OSD([subQ0]),TDD([makeQuery(id+"F28.imprint","IMPRINT",EDGE,{"disambiguationData":[TD([[makeQuery(id+"F28.imprint","INTERSECT",VERTEX,{"derivedFrom":[subQ0,sQuery(id+"F28.wireOp",EDGE,"E191")]}),1.0]])],"derivedFrom":subQ0})])],"isStart":false});}
            var Q2;
            {var subQ0=sQuery(id+"F28.wireOp",EDGE,"E189.right");Q2=makeQuery(id+"F30.opExtrude","CAP_EDGE",EDGE,{"disambiguationData":[OSD([subQ0]),TDD([makeQuery(id+"F28.imprint","IMPRINT",EDGE,{"disambiguationData":[TD([[makeQuery(id+"F28.imprint","INTERSECT",VERTEX,{"derivedFrom":[subQ0,sQuery(id+"F28.wireOp",EDGE,"E199.MirrorCS")]}),-1.0]])],"derivedFrom":subQ0})])],"isStart":false});}
            var Q3;
            {var subQ0=sQuery(id+"F28.wireOp",EDGE,"E189.left");Q3=makeQuery(id+"F30.opExtrude","CAP_EDGE",EDGE,{"disambiguationData":[OSD([subQ0]),TDD([makeQuery(id+"F28.imprint","IMPRINT",EDGE,{"disambiguationData":[TD([[makeQuery(id+"F28.imprint","INTERSECT",VERTEX,{"derivedFrom":[subQ0,sQuery(id+"F28.wireOp",EDGE,"E196.MirrorCS")]}),-1.0]])],"derivedFrom":subQ0})])],"isStart":false});}
            chamfer(context, id + "F31", {"entities" : qUnion([Q0, Q1, Q2, Q3]), "width" : 1.5 * mm, "tangentPropagation" : true});
        }
        {
            var Q0;
            Q0=makeQuery(id+"F28.imprint","IMPRINT",FACE,{"disambiguationData":[TD([[makeQuery(id+"F28.imprint","IMPRINT",EDGE,{"derivedFrom":sQuery(id+"F28.wireOp",EDGE,"E209")}),1.0]])]});
            extrude(context, id + "F32", {"entities" : qUnion([Q0]), "depth" : 10 * mm, "offsetDistance" : 25 * mm});
        }
        {
            var Q0;
            Q0=makeQuery(id+"F28.imprint","IMPRINT",FACE,{"disambiguationData":[TD([[makeQuery(id+"F28.imprint","IMPRINT",EDGE,{"derivedFrom":sQuery(id+"F28.wireOp",EDGE,"E208")}),1.0]])]});
            extrude(context, id + "F33", {"entities" : qUnion([Q0]), "operationType" : NewBodyOperationType.ADD, "depth" : 1 * mm, "offsetDistance" : 25 * mm});
        }
        {
            var Q0;
            Q0=makeQuery(id+"F32.opExtrude","CAP_EDGE",EDGE,{"disambiguationData":[OSD([sQuery(id+"F28.wireOp",EDGE,"E209")])],"isStart":false});
            chamfer(context, id + "F34", {"entities" : qUnion([Q0]), "width" : 1.5 * mm, "tangentPropagation" : true});
        }
    });
